# Revit family: Domotics-DomesticRanges-GEWISS-SYSTEM_BOX_WALL-MOUNTING_TOP
name_source: partatom
category: Apparecchi elettrici
revit_build: Autodesk Revit 2016 (Build: 20161004_0715(x64)
units: mm (PartAtom-declared; Revit-internal decimal feet)

## family parameters
Condiviso = Sì
Host = Superficie
Mantenere orientamento annotazione = No
Punto di calcolo locali = Sì
Quota connettore circolare = Usa diametro
Taglio con vuoti quando caricato = No
Tipo di parte = Normale

## types (1)
- Domotics-DomesticRanges-GEWISS-SYSTEM_BOX_WALL-MOUNTING_TOP
    Catalogue = DOMOTICS
    Catalogue Range = SYSTEM - BOXES
    Characteristics = Halogen free
    Colour = Cloud white
    Descrizione = TOP SYSTEM WALL ENC.PLATES 4PCLOUD WHITE
    EAN code = 8011564130227
    Electrocod = 0210
    For conduits max Ã˜ (mm) = 16 - 20
    For trunking dim. (mm) = 14x8.5 30x13 20x10
    Glow Wire Test = 650°C
    IDF = dac660ad-9b35-49b4-9ac1-50a97c30c20d
    IDT = 42988f69-0a41-4a44-8f66-de2be189585a
    Immagine tipo = GW22472.jpg
    Modello = GW22472
    Produttore = GEWISS S.p.A.
    Prospetto di default = 1219 mm
    SEO = Box
    Suitable for = 4 gang TOP SYSTEM
    Suitable for plates = 4 gang
    Technical sheet = https://www.gewiss.com
    Thermo-pressure with ball = 70
    Tipo = System Scatole Parete x Placche Top_GENERICO : GW22472 Scatola da parete per placche Top System 4P bianco nuvola
    URL = https://www.gewiss.com
    Version file RFA = 19.4

note: source unit labels omitted for Thermo-pressure with ball — the stored unit's dimension contradicts the parameter name (converter mislabeling)
